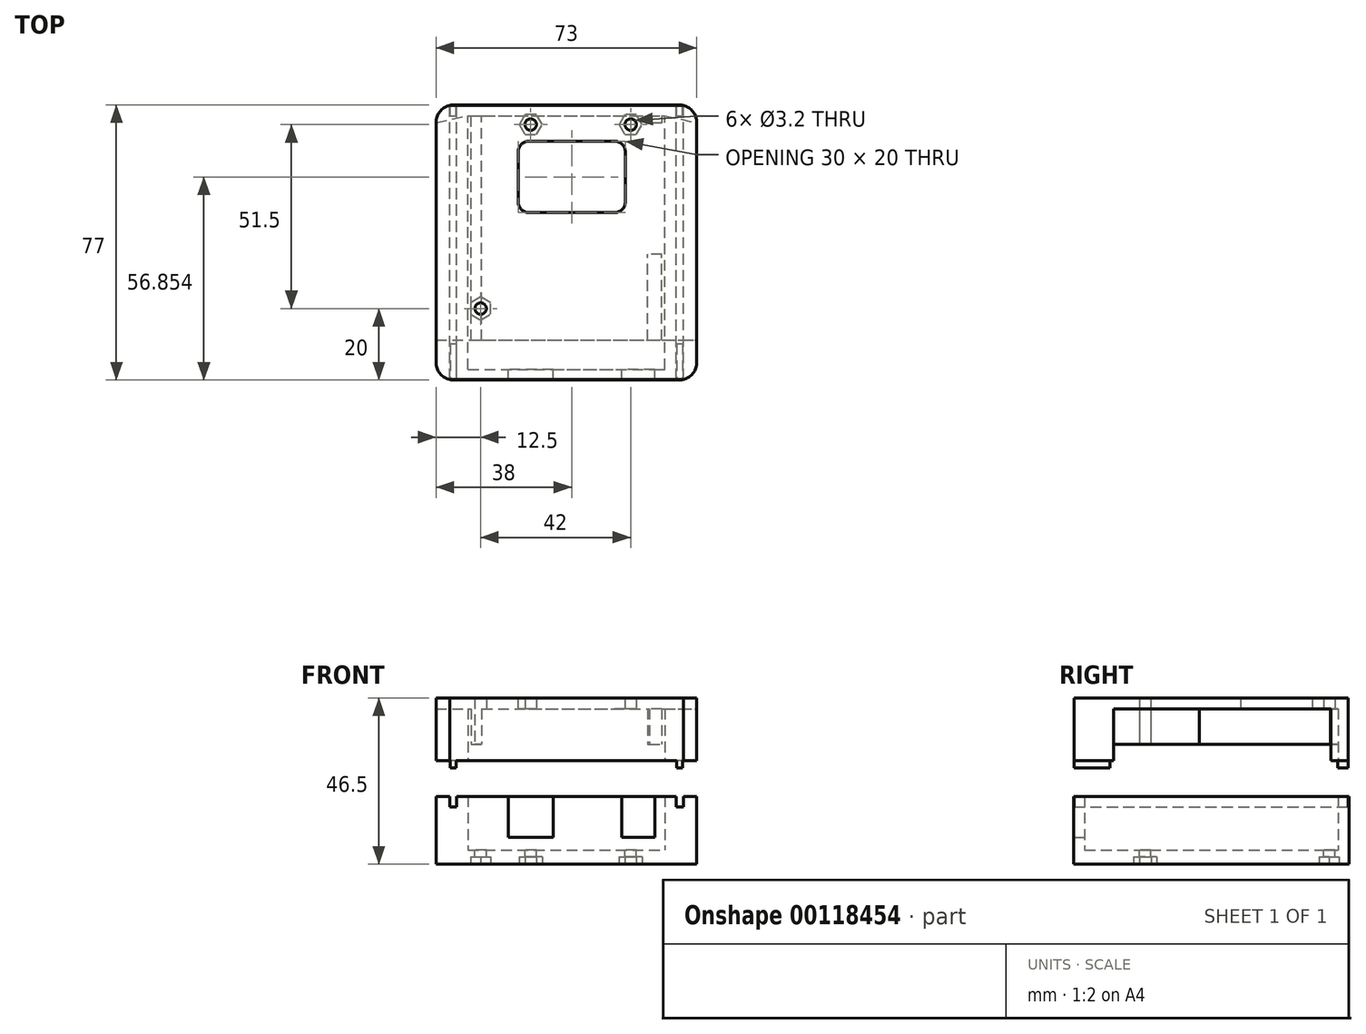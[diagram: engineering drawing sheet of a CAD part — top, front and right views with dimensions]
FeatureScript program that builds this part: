
annotation { "Feature Type Name" : "Feature", "Feature Type Description" : "" }
export const myFeature = defineFeature(function(context is Context, id is Id, definition is map)
    precondition{}
    {
        {
            var Q0;
            Q0=qCreatedBy(makeId("Top.planeOp"),FACE);
            var sketch = newSketch(context, id + "F0", { "sketchPlane" : qUnion([Q0])});
            skLineSegment(sketch, "E0.bottom", {"start": v(0, 0) * mm, "end": v(55, 0) * mm});
            skLineSegment(sketch, "E0.top", {"start": v(0, 71) * mm, "end": v(55, 71) * mm});
            skLineSegment(sketch, "E0.left", {"start": v(0, 0) * mm, "end": v(0, 71) * mm});
            skLineSegment(sketch, "E0.right", {"start": v(55, 0) * mm, "end": v(55, 71) * mm});
            skLineSegment(sketch, "E1.0", {"start": v(-3, 74) * mm, "end": v(58, 74) * mm});
            skLineSegment(sketch, "E1.1", {"start": v(-3, -3) * mm, "end": v(-3, 74) * mm});
            skLineSegment(sketch, "E1.2", {"start": v(-3, -3) * mm, "end": v(58, -3) * mm});
            skLineSegment(sketch, "E1.3", {"start": v(58, -3) * mm, "end": v(58, 74) * mm});
            skSolve(sketch);
        }
        {
            var Q0;
            Q0 = qSketchRegion(id + "F0", true);
            extrude(context, id + "F1", {"entities" : qUnion([Q0]), "depth" : 15 * mm});
        }
        {
            var Q0;
            Q0=makeQuery(id+"F1.opExtrude","CAP_FACE",FACE,{"disambiguationData":[OSD([sQuery(id+"F0.wireOp",EDGE,"E0.bottom"),sQuery(id+"F0.wireOp",EDGE,"E0.top"),sQuery(id+"F0.wireOp",EDGE,"E0.left"),sQuery(id+"F0.wireOp",EDGE,"E0.right"),sQuery(id+"F0.wireOp",EDGE,"E1.0"),sQuery(id+"F0.wireOp",EDGE,"E1.1"),sQuery(id+"F0.wireOp",EDGE,"E1.2"),sQuery(id+"F0.wireOp",EDGE,"E1.3")])],"isStart":true});
            var sketch = newSketch(context, id + "F2", { "sketchPlane" : qUnion([Q0])});
            skLineSegment(sketch, "E2.bottom", {"start": v(-3, -74) * mm, "end": v(58, -74) * mm});
            skLineSegment(sketch, "E2.top", {"start": v(-3, 3) * mm, "end": v(58, 3) * mm});
            skLineSegment(sketch, "E2.left", {"start": v(-3, -74) * mm, "end": v(-3, 3) * mm});
            skLineSegment(sketch, "E2.right", {"start": v(58, -74) * mm, "end": v(58, 3) * mm});
            skSolve(sketch);
        }
        {
            var Q0;
            Q0 = qSketchRegion(id + "F2", true);
            extrude(context, id + "F3", {"entities" : qUnion([Q0]), "operationType" : NewBodyOperationType.ADD, "depth" : 4 * mm});
        }
        {
            var Q0;
            Q0=makeQuery(id+"F3.opExtrude","CAP_FACE",FACE,{"disambiguationData":[OSD([sQuery(id+"F2.wireOp",EDGE,"E2.bottom"),sQuery(id+"F2.wireOp",EDGE,"E2.top"),sQuery(id+"F2.wireOp",EDGE,"E2.left"),sQuery(id+"F2.wireOp",EDGE,"E2.right")])],"isStart":true});
            var sketch = newSketch(context, id + "F4", { "sketchPlane" : qUnion([Q0])});
            skCircle(sketch, "E3", {"center": v(3.5, 17) * mm, "radius": 1.6 * mm});
            skCircle(sketch, "E4", {"center": v(45.5, 68.5) * mm, "radius": 1.6 * mm});
            skCircle(sketch, "E5", {"center": v(17.5, 68.5) * mm, "radius": 1.6 * mm});
            skSolve(sketch);
        }
        {
            var Q0;
            Q0 = qSketchRegion(id + "F4", true);
            extrude(context, id + "F5", {"entities" : qUnion([Q0]), "operationType" : NewBodyOperationType.REMOVE, "endBound" : BoundingType.THROUGH_ALL, "oppositeDirection" : true, "depth" : 25 * mm});
        }
        {
            var Q0;
            Q0=makeQuery(id+"F1.opExtrude","SWEPT_FACE",FACE,{"disambiguationData":[OSD([sQuery(id+"F0.wireOp",EDGE,"E0.bottom")])]});
            var sketch = newSketch(context, id + "F6", { "sketchPlane" : qUnion([Q0])});
            skLineSegment(sketch, "E6.bottom", {"start": v(-52.2, 15) * mm, "end": v(-43, 15) * mm});
            skLineSegment(sketch, "E6.top", {"start": v(-52.2, 3.5) * mm, "end": v(-43, 3.5) * mm});
            skLineSegment(sketch, "E6.left", {"start": v(-52.2, 15) * mm, "end": v(-52.2, 3.5) * mm});
            skLineSegment(sketch, "E6.right", {"start": v(-43, 15) * mm, "end": v(-43, 3.5) * mm});
            skLineSegment(sketch, "E7.bottom", {"start": v(-23.8, 15) * mm, "end": v(-11.2, 15) * mm});
            skLineSegment(sketch, "E7.top", {"start": v(-23.8, 3.5) * mm, "end": v(-11.2, 3.5) * mm});
            skLineSegment(sketch, "E7.left", {"start": v(-23.8, 15) * mm, "end": v(-23.8, 3.5) * mm});
            skLineSegment(sketch, "E7.right", {"start": v(-11.2, 15) * mm, "end": v(-11.2, 3.5) * mm});
            skSolve(sketch);
        }
        {
            var Q0;
            Q0 = qSketchRegion(id + "F6", true);
            extrude(context, id + "F7", {"entities" : qUnion([Q0]), "operationType" : NewBodyOperationType.REMOVE, "endBound" : BoundingType.THROUGH_ALL, "oppositeDirection" : true, "depth" : 25 * mm});
        }
        {
            var Q0;
            Q0=makeQuery(id+"FIKg3vUpQGRYwgF_1.boolean.opBoolean","MERGE",FACE,{"derivedFrom":[makeQuery(id+"F3.opExtrude","CAP_FACE",FACE,{"disambiguationData":[OSD([sQuery(id+"F2.wireOp",EDGE,"E2.bottom"),sQuery(id+"F2.wireOp",EDGE,"E2.top"),sQuery(id+"F2.wireOp",EDGE,"E2.left"),sQuery(id+"F2.wireOp",EDGE,"E2.right")])],"isStart":false}),makeQuery(id+"FIKg3vUpQGRYwgF_1.opExtrude","CAP_FACE",FACE,{"disambiguationData":[OSD([sQuery(id+"FjnMTyNSBjaQ7zO_1.wireOp",EDGE,"I8RTsVfb-v8po-NAC8-c6id-qPJGLXU0blO0"),sQuery(id+"FjnMTyNSBjaQ7zO_1.wireOp",EDGE,"TOZflPdF-oIzK-XCOg-TYKf-1P7zer94MZVB"),sQuery(id+"FjnMTyNSBjaQ7zO_1.wireOp",EDGE,"pYX2pmDH-hO49-54TM-vNzi-nz8wKM9bPT5e"),sQuery(id+"FjnMTyNSBjaQ7zO_1.wireOp",EDGE,"MglhZEiD-R0rR-m8Tz-A3Ae-5PCLMhfcjgwQ")])],"isStart":false}),makeQuery(id+"FIKg3vUpQGRYwgF_1.opExtrude","CAP_FACE",FACE,{"disambiguationData":[OSD([sQuery(id+"FjnMTyNSBjaQ7zO_1.wireOp",EDGE,"vS74dPrh-Yngv-g6sy-3JaW-diKomyqy4hrZ"),sQuery(id+"FjnMTyNSBjaQ7zO_1.wireOp",EDGE,"dBJddLBu-svfx-fSTK-aqw2-g9uQsKwWNiIV"),sQuery(id+"FjnMTyNSBjaQ7zO_1.wireOp",EDGE,"ezTkL4eV-m3gI-EGRE-anRO-PJIIp1dLkXKT"),sQuery(id+"FjnMTyNSBjaQ7zO_1.wireOp",EDGE,"nig95sQ7-wmuy-74uW-rtDo-H4HC6JsRILze")])],"isStart":false})]});
            var sketch = newSketch(context, id + "F8", { "sketchPlane" : qUnion([Q0])});
            skCircle(sketch, "E8.cCircle", {"center": v(3.5, -17) * mm, "radius": 2.8 * mm, "construction": true});
            skLineSegment(sketch, "E8.0", {"start": v(6.3, -15.38) * mm, "end": v(6.3, -18.62) * mm});
            skLineSegment(sketch, "E8.1", {"start": v(6.3, -18.62) * mm, "end": v(3.5, -20.23) * mm});
            skLineSegment(sketch, "E8.2", {"start": v(3.5, -20.23) * mm, "end": v(0.7, -18.62) * mm});
            skLineSegment(sketch, "E8.3", {"start": v(0.7, -18.62) * mm, "end": v(0.7, -15.38) * mm});
            skLineSegment(sketch, "E8.4", {"start": v(0.7, -15.38) * mm, "end": v(3.5, -13.77) * mm});
            skLineSegment(sketch, "E8.5", {"start": v(3.5, -13.77) * mm, "end": v(6.3, -15.38) * mm});
            skPoint(sketch, "E8.0.midPoint", {"position": v(6.3, -17) * mm});
            skCircle(sketch, "E9.cCircle", {"center": v(17.5, -68.5) * mm, "radius": 2.8 * mm, "construction": true});
            skLineSegment(sketch, "E9.0", {"start": v(19.12, -71.3) * mm, "end": v(15.88, -71.3) * mm});
            skLineSegment(sketch, "E9.1", {"start": v(15.88, -71.3) * mm, "end": v(14.27, -68.5) * mm});
            skLineSegment(sketch, "E9.2", {"start": v(14.27, -68.5) * mm, "end": v(15.88, -65.7) * mm});
            skLineSegment(sketch, "E9.3", {"start": v(15.88, -65.7) * mm, "end": v(19.12, -65.7) * mm});
            skLineSegment(sketch, "E9.4", {"start": v(19.12, -65.7) * mm, "end": v(20.73, -68.5) * mm});
            skLineSegment(sketch, "E9.5", {"start": v(20.73, -68.5) * mm, "end": v(19.12, -71.3) * mm});
            skPoint(sketch, "E9.0.midPoint", {"position": v(17.5, -71.3) * mm});
            skCircle(sketch, "E10.cCircle", {"center": v(45.5, -68.5) * mm, "radius": 2.8 * mm, "construction": true});
            skLineSegment(sketch, "E10.0", {"start": v(47.12, -71.3) * mm, "end": v(43.88, -71.3) * mm});
            skLineSegment(sketch, "E10.1", {"start": v(43.88, -71.3) * mm, "end": v(42.27, -68.5) * mm});
            skLineSegment(sketch, "E10.2", {"start": v(42.27, -68.5) * mm, "end": v(43.88, -65.7) * mm});
            skLineSegment(sketch, "E10.3", {"start": v(43.88, -65.7) * mm, "end": v(47.12, -65.7) * mm});
            skLineSegment(sketch, "E10.4", {"start": v(47.12, -65.7) * mm, "end": v(48.73, -68.5) * mm});
            skLineSegment(sketch, "E10.5", {"start": v(48.73, -68.5) * mm, "end": v(47.12, -71.3) * mm});
            skPoint(sketch, "E10.0.midPoint", {"position": v(45.5, -71.3) * mm});
            skSolve(sketch);
        }
        {
            var Q0;
            Q0 = qSketchRegion(id + "F8", true);
            extrude(context, id + "F9", {"entities" : qUnion([Q0]), "operationType" : NewBodyOperationType.REMOVE, "oppositeDirection" : true, "depth" : 2 * mm});
        }
        {
            var Q0;
            Q0=makeQuery(id+"F3.boolean.opBoolean","MERGE",FACE,{"derivedFrom":[makeQuery(id+"F1.opExtrude","SWEPT_FACE",FACE,{"disambiguationData":[OSD([sQuery(id+"F0.wireOp",EDGE,"E1.0")])]}),makeQuery(id+"F3.opExtrude","SWEPT_FACE",FACE,{"disambiguationData":[OSD([sQuery(id+"F2.wireOp",EDGE,"E2.bottom")])]})]});
            var sketch = newSketch(context, id + "F10", { "sketchPlane" : qUnion([Q0])});
            skLineSegment(sketch, "E11.bottom", {"start": v(-58, 15) * mm, "end": v(-58.2, 15) * mm});
            skLineSegment(sketch, "E11.top", {"start": v(-58, -4) * mm, "end": v(-64, -4) * mm});
            skLineSegment(sketch, "E11.left", {"start": v(-58, 15) * mm, "end": v(-58, -4) * mm});
            skLineSegment(sketch, "E11.right", {"start": v(-64, 15) * mm, "end": v(-64, -4) * mm});
            skLineSegment(sketch, "E12.top", {"start": v(-60.2, 12) * mm, "end": v(-58.2, 12) * mm});
            skLineSegment(sketch, "E12.left", {"start": v(-60.2, 15) * mm, "end": v(-60.2, 12) * mm});
            skLineSegment(sketch, "E12.right", {"start": v(-58.2, 15) * mm, "end": v(-58.2, 12) * mm});
            skLineSegment(sketch, "E13", {"start": v(-27.5, -4) * mm, "end": v(-27.5, 15) * mm});
            skLineSegment(sketch, "E14.trimOffspring", {"start": v(-60.2, 15) * mm, "end": v(-64, 15) * mm});
            skLineSegment(sketch, "E15.MirrorCS", {"start": v(3, 15) * mm, "end": v(3.2, 15) * mm});
            skLineSegment(sketch, "E16.MirrorCS", {"start": v(5.2, 12) * mm, "end": v(3.2, 12) * mm});
            skLineSegment(sketch, "E17.MirrorCS", {"start": v(5.2, 15) * mm, "end": v(5.2, 12) * mm});
            skLineSegment(sketch, "E18.MirrorCS", {"start": v(3.2, 15) * mm, "end": v(3.2, 12) * mm});
            skLineSegment(sketch, "E19.MirrorCS", {"start": v(3, -4) * mm, "end": v(9, -4) * mm});
            skLineSegment(sketch, "E20.MirrorCS", {"start": v(3, 15) * mm, "end": v(3, -4) * mm});
            skLineSegment(sketch, "E21.MirrorCS", {"start": v(5.2, 15) * mm, "end": v(9, 15) * mm});
            skLineSegment(sketch, "E22.MirrorCS", {"start": v(9, 15) * mm, "end": v(9, -4) * mm});
            skSolve(sketch);
        }
        {
            var Q0;
            Q0 = qSketchRegion(id + "F10", true);
            extrude(context, id + "F11", {"entities" : qUnion([Q0]), "operationType" : NewBodyOperationType.ADD, "oppositeDirection" : true, "depth" : 77 * mm});
        }
        {
            var Q0;
            Q0=makeQuery(id+"F11.opExtrude","CAP_EDGE",EDGE,{"disambiguationData":[OSD([sQuery(id+"F10.wireOp",EDGE,"1212b732-435f-4440-8f70-73e77841f30e5.MirrorCS")])],"isStart":true});
            var Q1;
            Q1=makeQuery(id+"F11.opExtrude","CAP_EDGE",EDGE,{"disambiguationData":[OSD([sQuery(id+"F10.wireOp",EDGE,"E11.right")])],"isStart":true});
            var Q2;
            Q2=makeQuery(id+"F11.opExtrude","CAP_EDGE",EDGE,{"disambiguationData":[OSD([sQuery(id+"F10.wireOp",EDGE,"E11.right")])],"isStart":false});
            var Q3;
            Q3=makeQuery(id+"F11.opExtrude","CAP_EDGE",EDGE,{"disambiguationData":[OSD([sQuery(id+"F10.wireOp",EDGE,"1212b732-435f-4440-8f70-73e77841f30e5.MirrorCS")])],"isStart":false});
            var Q4;
            Q4=makeQuery(id+"F11.opExtrude","CAP_EDGE",EDGE,{"disambiguationData":[OSD([sQuery(id+"F10.wireOp",EDGE,"E22.MirrorCS")])],"isStart":true});
            var Q5;
            Q5=makeQuery(id+"F11.opExtrude","CAP_EDGE",EDGE,{"disambiguationData":[OSD([sQuery(id+"F10.wireOp",EDGE,"E22.MirrorCS")])],"isStart":false});
            fillet(context, id + "F12", {"entities" : qUnion([Q0, Q1, Q2, Q3, Q4, Q5]), "radius" : 5 * mm, "tangentPropagation" : true, "allowEdgeOverflow" : false});
        }
        {
            var Q0;
            Q0=qCreatedBy(makeId("Top.planeOp"),FACE);
            cPlane(context, id + "F13", {"entities" : qUnion([Q0]), "cplaneType" : CPlaneType.OFFSET, "offset" : 25 * mm, "width" : 150 * mm, "height" : 150 * mm});
        }
        {
            var Q0;
            Q0=qCreatedBy(id+"F13.planeOp",FACE);
            var sketch = newSketch(context, id + "F14", { "sketchPlane" : qUnion([Q0])});
            skArc(sketch, "E23.0", {"start": v(64, 69) * mm, "mid": v(62.94, 72.08) * mm, "end": v(60.2, 73.85) * mm});
            skArc(sketch, "E24.0", {"start": v(-5.2, 73.85) * mm, "mid": v(-7.94, 72.08) * mm, "end": v(-9, 69) * mm});
            skArc(sketch, "E25.0", {"start": v(60.2, -2.85) * mm, "mid": v(62.94, -1.08) * mm, "end": v(64, 2) * mm});
            skArc(sketch, "E26.0", {"start": v(-9, 2) * mm, "mid": v(-7.94, -1.08) * mm, "end": v(-5.2, -2.85) * mm});
            skLineSegment(sketch, "E27", {"start": v(64, 8.15) * mm, "end": v(64, 2) * mm});
            skLineSegment(sketch, "E28", {"start": v(60.2, 73.85) * mm, "end": v(-5.2, 73.85) * mm});
            skLineSegment(sketch, "E29", {"start": v(-9, 8.15) * mm, "end": v(-9, 2) * mm});
            skLineSegment(sketch, "E30", {"start": v(-5.2, -2.85) * mm, "end": v(60.2, -2.85) * mm});
            skLineSegment(sketch, "E31", {"start": v(-9, 69) * mm, "end": v(0, 71) * mm});
            skLineSegment(sketch, "E32", {"start": v(0, 71) * mm, "end": v(55, 71) * mm});
            skLineSegment(sketch, "E33", {"start": v(55, 71) * mm, "end": v(64, 69) * mm});
            skLineSegment(sketch, "E34", {"start": v(-9, 8.15) * mm, "end": v(64, 8.15) * mm});
            skSolve(sketch);
        }
        {
            var Q0;
            Q0 = qSketchRegion(id + "F14", true);
            extrude(context, id + "F15", {"entities" : qUnion([Q0]), "depth" : 4.5 * mm});
        }
        {
            var Q0;
            Q0=makeQuery(id+"F15.opExtrude","SWEPT_FACE",FACE,{"disambiguationData":[OSD([sQuery(id+"F14.wireOp",EDGE,"E30")])]});
            var sketch = newSketch(context, id + "F16", { "sketchPlane" : qUnion([Q0])});
            skLineSegment(sketch, "E35", {"start": v(-5, 25) * mm, "end": v(-5, 23) * mm});
            skLineSegment(sketch, "E36", {"start": v(-5, 23) * mm, "end": v(-3.4, 23) * mm});
            skLineSegment(sketch, "E37", {"start": v(-3.4, 23) * mm, "end": v(-3.4, 25) * mm});
            skLineSegment(sketch, "E38", {"start": v(-3.4, 25) * mm, "end": v(-5, 25) * mm});
            skLineSegment(sketch, "E39", {"start": v(58.4, 25) * mm, "end": v(58.4, 23) * mm});
            skLineSegment(sketch, "E40", {"start": v(58.4, 23) * mm, "end": v(60, 23) * mm});
            skLineSegment(sketch, "E41", {"start": v(60, 23) * mm, "end": v(60, 25) * mm});
            skLineSegment(sketch, "E42", {"start": v(60, 25) * mm, "end": v(58.4, 25) * mm});
            skSolve(sketch);
        }
        {
            var Q0;
            Q0 = qSketchRegion(id + "F16", true);
            extrude(context, id + "F17", {"entities" : qUnion([Q0]), "operationType" : NewBodyOperationType.ADD, "oppositeDirection" : true, "depth" : 10 * mm});
        }
        {
            var Q0;
            Q0=makeQuery(id+"F15.opExtrude","SWEPT_FACE",FACE,{"disambiguationData":[OSD([sQuery(id+"F14.wireOp",EDGE,"E28")])]});
            var sketch = newSketch(context, id + "F18", { "sketchPlane" : qUnion([Q0])});
            skLineSegment(sketch, "E43.bottom", {"start": v(-60, 23) * mm, "end": v(-58.4, 23) * mm});
            skLineSegment(sketch, "E43.top", {"start": v(-60, 25) * mm, "end": v(-58.4, 25) * mm});
            skLineSegment(sketch, "E43.left", {"start": v(-60, 23) * mm, "end": v(-60, 25) * mm});
            skLineSegment(sketch, "E43.right", {"start": v(-58.4, 23) * mm, "end": v(-58.4, 25) * mm});
            skLineSegment(sketch, "E44.bottom", {"start": v(3.4, 25) * mm, "end": v(5, 25) * mm});
            skLineSegment(sketch, "E44.top", {"start": v(3.4, 23) * mm, "end": v(5, 23) * mm});
            skLineSegment(sketch, "E44.left", {"start": v(3.4, 25) * mm, "end": v(3.4, 23) * mm});
            skLineSegment(sketch, "E44.right", {"start": v(5, 25) * mm, "end": v(5, 23) * mm});
            skSolve(sketch);
        }
        {
            var Q0;
            Q0 = qSketchRegion(id + "F18", true);
            extrude(context, id + "F19", {"entities" : qUnion([Q0]), "operationType" : NewBodyOperationType.ADD, "oppositeDirection" : true, "depth" : 3 * mm});
        }
        {
            var Q0;
            Q0=makeQuery(id+"F15.opExtrude","CAP_FACE",FACE,{"disambiguationData":[OSD([sQuery(id+"F14.wireOp",EDGE,"E25.0"),sQuery(id+"F14.wireOp",EDGE,"E26.0"),sQuery(id+"F14.wireOp",EDGE,"E27"),sQuery(id+"F14.wireOp",EDGE,"E29"),sQuery(id+"F14.wireOp",EDGE,"E30"),sQuery(id+"F14.wireOp",EDGE,"E34")])],"isStart":false});
            var sketch = newSketch(context, id + "F20", { "sketchPlane" : qUnion([Q0])});
            skLineSegment(sketch, "E45.bottom", {"start": v(0.8, -2.85) * mm, "end": v(3.8, -2.85) * mm});
            skLineSegment(sketch, "E45.top", {"start": v(0.8, 73.85) * mm, "end": v(3.8, 73.85) * mm});
            skLineSegment(sketch, "E45.left", {"start": v(0.8, -2.85) * mm, "end": v(0.8, 73.85) * mm});
            skLineSegment(sketch, "E45.right", {"start": v(3.8, -2.85) * mm, "end": v(3.8, 73.85) * mm});
            skLineSegment(sketch, "E46.bottom", {"start": v(54.2, -2.85) * mm, "end": v(50.2, -2.85) * mm});
            skLineSegment(sketch, "E46.top", {"start": v(54.2, 32.15) * mm, "end": v(50.2, 32.15) * mm});
            skLineSegment(sketch, "E46.left", {"start": v(54.2, -2.85) * mm, "end": v(54.2, 32.15) * mm});
            skLineSegment(sketch, "E46.right", {"start": v(50.2, -2.85) * mm, "end": v(50.2, 32.15) * mm});
            skLineSegment(sketch, "E47.bottom", {"start": v(54.2, 73.85) * mm, "end": v(50.7, 73.85) * mm});
            skLineSegment(sketch, "E47.top", {"start": v(54.2, 68.85) * mm, "end": v(50.7, 68.85) * mm});
            skLineSegment(sketch, "E47.left", {"start": v(54.2, 73.85) * mm, "end": v(54.2, 68.85) * mm});
            skLineSegment(sketch, "E47.right", {"start": v(50.7, 73.85) * mm, "end": v(50.7, 68.85) * mm});
            skSolve(sketch);
        }
        {
            var Q0;
            Q0 = qSketchRegion(id + "F20", true);
            extrude(context, id + "F21", {"entities" : qUnion([Q0]), "operationType" : NewBodyOperationType.ADD, "depth" : 10 * mm});
        }
        {
            var Q0;
            Q0=makeQuery(id+"F21.opExtrude","CAP_FACE",FACE,{"disambiguationData":[OSD([sQuery(id+"F20.wireOp",EDGE,"E45.bottom"),sQuery(id+"F20.wireOp",EDGE,"E45.top"),sQuery(id+"F20.wireOp",EDGE,"E45.left"),sQuery(id+"F20.wireOp",EDGE,"E45.right")])],"isStart":false});
            var sketch = newSketch(context, id + "F22", { "sketchPlane" : qUnion([Q0])});
            skLineSegment(sketch, "E48.0", {"start": v(64, 2) * mm, "end": v(64, 69) * mm});
            skArc(sketch, "E48.1", {"start": v(60.2, -2.85) * mm, "mid": v(62.94, -1.08) * mm, "end": v(64, 2) * mm});
            skArc(sketch, "E48.2", {"start": v(64, 69) * mm, "mid": v(62.94, 72.08) * mm, "end": v(60.2, 73.85) * mm});
            skLineSegment(sketch, "E48.3", {"start": v(-5.2, -2.85) * mm, "end": v(60.2, -2.85) * mm});
            skLineSegment(sketch, "E48.4", {"start": v(60.2, 73.85) * mm, "end": v(-5.2, 73.85) * mm});
            skArc(sketch, "E48.5", {"start": v(-5.2, 73.85) * mm, "mid": v(-7.94, 72.08) * mm, "end": v(-9, 69) * mm});
            skLineSegment(sketch, "E48.6", {"start": v(-9, 2) * mm, "end": v(-9, 69) * mm});
            skArc(sketch, "E48.7", {"start": v(-9, 2) * mm, "mid": v(-7.94, -1.08) * mm, "end": v(-5.2, -2.85) * mm});
            skSolve(sketch);
        }
        {
            var Q0;
            Q0 = qSketchRegion(id + "F22", true);
            extrude(context, id + "F23", {"entities" : qUnion([Q0]), "operationType" : NewBodyOperationType.ADD, "depth" : 3 * mm});
        }
        {
            var Q0;
            Q0=makeQuery(id+"F15.opExtrude","CAP_FACE",FACE,{"disambiguationData":[OSD([sQuery(id+"F14.wireOp",EDGE,"E25.0"),sQuery(id+"F14.wireOp",EDGE,"E26.0"),sQuery(id+"F14.wireOp",EDGE,"E27"),sQuery(id+"F14.wireOp",EDGE,"E29"),sQuery(id+"F14.wireOp",EDGE,"E30"),sQuery(id+"F14.wireOp",EDGE,"E34")])],"isStart":false});
            extrude(context, id + "F24", {"entities" : qUnion([Q0]), "operationType" : NewBodyOperationType.ADD, "endBound" : BoundingType.UP_TO_NEXT, "depth" : 25 * mm});
        }
        {
            var Q0;
            Q0=makeQuery(id+"F15.opExtrude","CAP_FACE",FACE,{"disambiguationData":[OSD([sQuery(id+"F14.wireOp",EDGE,"E23.0"),sQuery(id+"F14.wireOp",EDGE,"E24.0"),sQuery(id+"F14.wireOp",EDGE,"E28"),sQuery(id+"F14.wireOp",EDGE,"E31"),sQuery(id+"F14.wireOp",EDGE,"E32"),sQuery(id+"F14.wireOp",EDGE,"E33")])],"isStart":false});
            extrude(context, id + "F25", {"entities" : qUnion([Q0]), "operationType" : NewBodyOperationType.ADD, "endBound" : BoundingType.UP_TO_NEXT, "depth" : 25 * mm});
        }
        {
            var Q0;
            Q0=makeQuery(id+"F11.boolean.opBoolean","MERGE",FACE,{"derivedFrom":[makeQuery(id+"F3.opExtrude","CAP_FACE",FACE,{"disambiguationData":[OSD([sQuery(id+"F2.wireOp",EDGE,"E2.bottom"),sQuery(id+"F2.wireOp",EDGE,"E2.top"),sQuery(id+"F2.wireOp",EDGE,"E2.left"),sQuery(id+"F2.wireOp",EDGE,"E2.right")])],"isStart":false}),makeQuery(id+"F11.opExtrude","SWEPT_FACE",FACE,{"disambiguationData":[OSD([sQuery(id+"F10.wireOp",EDGE,"E11.top")])]}),makeQuery(id+"F11.opExtrude","SWEPT_FACE",FACE,{"disambiguationData":[OSD([sQuery(id+"F10.wireOp",EDGE,"E19.MirrorCS")])]})]});
            var sketch = newSketch(context, id + "F26", { "sketchPlane" : qUnion([Q0])});
            skCircle(sketch, "E49.0", {"center": v(45.5, -68.5) * mm, "radius": 1.6 * mm});
            skCircle(sketch, "E50.0", {"center": v(17.5, -68.5) * mm, "radius": 1.6 * mm});
            skCircle(sketch, "E51.0", {"center": v(3.5, -17) * mm, "radius": 1.6 * mm});
            skSolve(sketch);
        }
        {
            var Q0;
            Q0 = qSketchRegion(id + "F26", true);
            extrude(context, id + "F27", {"entities" : qUnion([Q0]), "operationType" : NewBodyOperationType.REMOVE, "endBound" : BoundingType.THROUGH_ALL, "oppositeDirection" : true, "depth" : 25 * mm});
        }
        {
            var Q0;
            Q0=makeQuery(id+"F23.opExtrude","CAP_FACE",FACE,{"disambiguationData":[OSD([sQuery(id+"F22.wireOp",EDGE,"E48.0"),sQuery(id+"F22.wireOp",EDGE,"E48.1"),sQuery(id+"F22.wireOp",EDGE,"E48.2"),sQuery(id+"F22.wireOp",EDGE,"E48.3"),sQuery(id+"F22.wireOp",EDGE,"E48.4"),sQuery(id+"F22.wireOp",EDGE,"E48.5"),sQuery(id+"F22.wireOp",EDGE,"E48.6"),sQuery(id+"F22.wireOp",EDGE,"E48.7")])],"isStart":false});
            var sketch = newSketch(context, id + "F28", { "sketchPlane" : qUnion([Q0])});
            skLineSegment(sketch, "E52.bottom", {"start": v(17, 63.85) * mm, "end": v(41, 63.85) * mm});
            skLineSegment(sketch, "E52.top", {"start": v(17, 43.85) * mm, "end": v(41, 43.85) * mm});
            skLineSegment(sketch, "E52.left", {"start": v(14, 60.85) * mm, "end": v(14, 46.85) * mm});
            skLineSegment(sketch, "E52.right", {"start": v(44, 60.85) * mm, "end": v(44, 46.85) * mm});
            skPoint(sketch, "E53.visualSharp", {"position": v(14, 63.85) * mm});
            skArc(sketch, "E53.filletArc", {"start": v(17, 63.85) * mm, "mid": v(14.88, 62.98) * mm, "end": v(14, 60.85) * mm});
            skPoint(sketch, "E54.visualSharp", {"position": v(44, 63.85) * mm});
            skArc(sketch, "E54.filletArc", {"start": v(44, 60.85) * mm, "mid": v(43.12, 62.98) * mm, "end": v(41, 63.85) * mm});
            skPoint(sketch, "E55.visualSharp", {"position": v(44, 43.85) * mm});
            skArc(sketch, "E55.filletArc", {"start": v(41, 43.85) * mm, "mid": v(43.12, 44.73) * mm, "end": v(44, 46.85) * mm});
            skPoint(sketch, "E56.visualSharp", {"position": v(14, 43.85) * mm});
            skArc(sketch, "E56.filletArc", {"start": v(14, 46.85) * mm, "mid": v(14.88, 44.73) * mm, "end": v(17, 43.85) * mm});
            skSolve(sketch);
        }
        {
            var Q0;
            Q0 = qSketchRegion(id + "F28", true);
            extrude(context, id + "F29", {"entities" : qUnion([Q0]), "operationType" : NewBodyOperationType.REMOVE, "oppositeDirection" : true, "depth" : 25 * mm});
        }
    });
